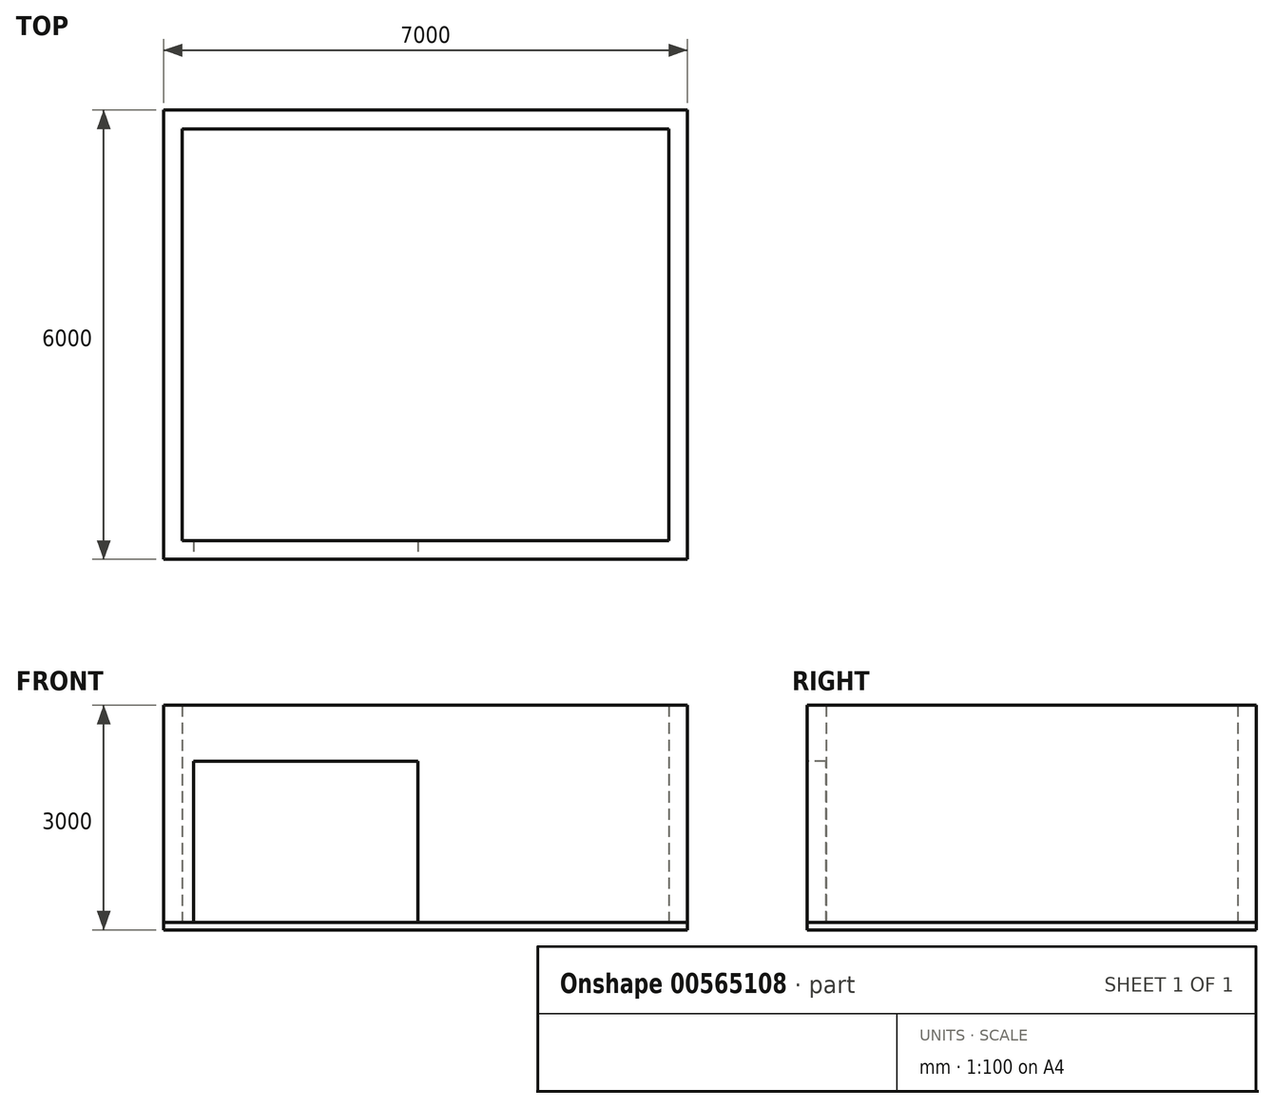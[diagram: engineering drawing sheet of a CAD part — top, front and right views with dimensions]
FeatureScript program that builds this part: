
annotation { "Feature Type Name" : "Feature", "Feature Type Description" : "" }
export const myFeature = defineFeature(function(context is Context, id is Id, definition is map)
    precondition{}
    {
        {
            var Q0;
            Q0=qCreatedBy(makeId("Top.planeOp"),FACE);
            var sketch = newSketch(context, id + "F0", { "sketchPlane" : qUnion([Q0])});
            skLineSegment(sketch, "E0.bottom", {"start": v(-3500, 3000) * mm, "end": v(3500, 3000) * mm});
            skLineSegment(sketch, "E0.top", {"start": v(-3500, -3000) * mm, "end": v(3500, -3000) * mm});
            skLineSegment(sketch, "E0.left", {"start": v(-3500, 3000) * mm, "end": v(-3500, -3000) * mm});
            skLineSegment(sketch, "E0.right", {"start": v(3500, 3000) * mm, "end": v(3500, -3000) * mm});
            skPoint(sketch, "E0.middle", {"position": v(0, 0) * mm});
            skSolve(sketch);
        }
        {
            var Q0;
            Q0=makeQuery(id+"F0.imprint","IMPRINT",FACE,{"disambiguationData":[TD([[makeQuery(id+"F0.imprint","IMPRINT",EDGE,{"derivedFrom":sQuery(id+"F0.wireOp",EDGE,"E0.bottom")}),-1.0]])]});
            extrude(context, id + "F1", {"entities" : qUnion([Q0]), "depth" : 100 * mm, "offsetDistance" : 25 * mm});
        }
        {
            var Q0;
            Q0=makeQuery(id+"F1.opExtrude","CAP_FACE",FACE,{"disambiguationData":[OSD([sQuery(id+"F0.wireOp",EDGE,"E0.bottom"),sQuery(id+"F0.wireOp",EDGE,"E0.top"),sQuery(id+"F0.wireOp",EDGE,"E0.left"),sQuery(id+"F0.wireOp",EDGE,"E0.right")])],"isStart":false});
            var sketch = newSketch(context, id + "F2", { "sketchPlane" : qUnion([Q0])});
            skLineSegment(sketch, "E1.0.0", {"start": v(-3500, 3000) * mm, "end": v(-3500, -3000) * mm});
            skLineSegment(sketch, "E1.0.1", {"start": v(-3500, -3000) * mm, "end": v(3500, -3000) * mm});
            skLineSegment(sketch, "E1.0.2", {"start": v(3500, -3000) * mm, "end": v(3500, 3000) * mm});
            skLineSegment(sketch, "E1.0.3", {"start": v(3500, 3000) * mm, "end": v(-3500, 3000) * mm});
            skLineSegment(sketch, "E2.0", {"start": v(-3250, 2750) * mm, "end": v(-3250, -2750) * mm});
            skLineSegment(sketch, "E2.1", {"start": v(3250, 2750) * mm, "end": v(-3250, 2750) * mm});
            skLineSegment(sketch, "E2.2", {"start": v(3250, -2750) * mm, "end": v(3250, 2750) * mm});
            skLineSegment(sketch, "E2.3", {"start": v(-3250, -2750) * mm, "end": v(3250, -2750) * mm});
            skSolve(sketch);
        }
        {
            var Q0;
            Q0 = qSketchRegion(id + "F2", true);
            extrude(context, id + "F3", {"entities" : qUnion([Q0]), "depth" : (3000 - 100) * mm, "offsetDistance" : 25 * mm});
        }
        {
            var Q0;
            Q0=makeQuery(id+"F3.opExtrude","SWEPT_FACE",FACE,{"disambiguationData":[OSD([sQuery(id+"F2.wireOp",EDGE,"E1.0.1")])]});
            var sketch = newSketch(context, id + "F4", { "sketchPlane" : qUnion([Q0])});
            skLineSegment(sketch, "E3.bottom", {"start": v(-3100, 100) * mm, "end": v(-100, 100) * mm});
            skLineSegment(sketch, "E3.top", {"start": v(-3100, 2250) * mm, "end": v(-100, 2250) * mm});
            skLineSegment(sketch, "E3.left", {"start": v(-3100, 100) * mm, "end": v(-3100, 2250) * mm});
            skLineSegment(sketch, "E3.right", {"start": v(-100, 100) * mm, "end": v(-100, 2250) * mm});
            skSolve(sketch);
        }
        {
            var Q0;
            Q0 = qSketchRegion(id + "F4", true);
            extrude(context, id + "F5", {"entities" : qUnion([Q0]), "operationType" : NewBodyOperationType.REMOVE, "endBound" : BoundingType.UP_TO_NEXT, "oppositeDirection" : true, "depth" : 25 * mm, "offsetDistance" : 25 * mm});
        }
    });
